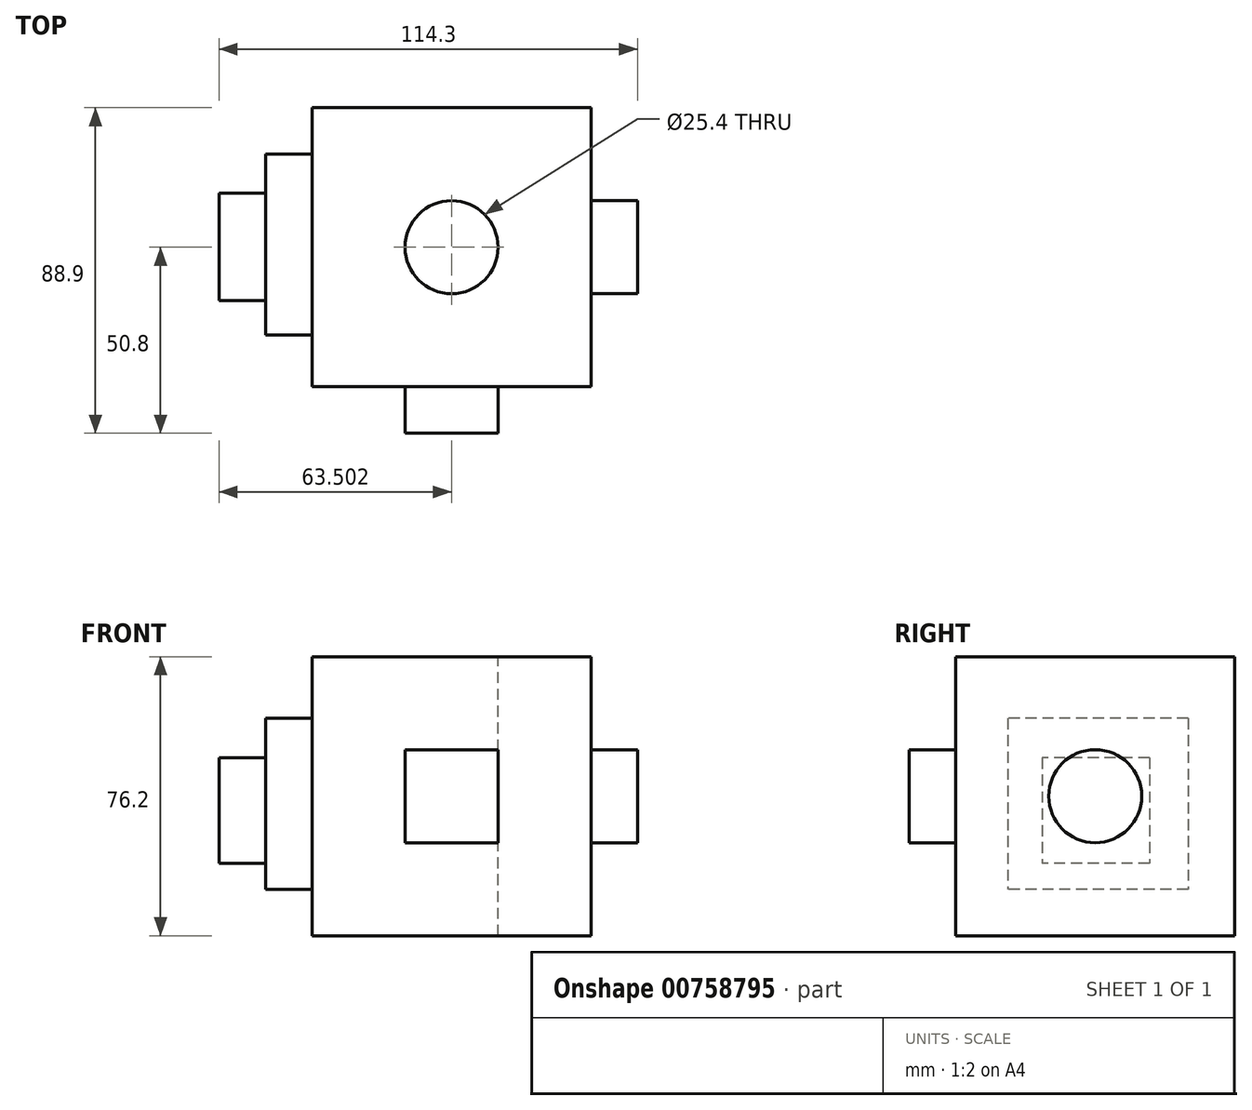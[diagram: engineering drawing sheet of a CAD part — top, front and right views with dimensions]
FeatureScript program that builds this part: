
annotation { "Feature Type Name" : "Feature", "Feature Type Description" : "" }
export const myFeature = defineFeature(function(context is Context, id is Id, definition is map)
    precondition{}
    {
        {
            var Q0;
            Q0=qCreatedBy(makeId("Front.planeOp"),FACE);
            var sketch = newSketch(context, id + "F0", { "sketchPlane" : qUnion([Q0])});
            skLineSegment(sketch, "E0.bottom", {"start": v(-34.38, 38.32) * mm, "end": v(41.82, 38.32) * mm});
            skLineSegment(sketch, "E0.top", {"start": v(-34.38, -37.88) * mm, "end": v(41.82, -37.88) * mm});
            skLineSegment(sketch, "E0.left", {"start": v(-34.38, 38.32) * mm, "end": v(-34.38, -37.88) * mm});
            skLineSegment(sketch, "E0.right", {"start": v(41.82, 38.32) * mm, "end": v(41.82, -37.88) * mm});
            skSolve(sketch);
        }
        {
            var Q0;
            Q0=makeQuery(id+"F0.imprint","IMPRINT",FACE,{"disambiguationData":[TD([[makeQuery(id+"F0.imprint","IMPRINT",EDGE,{"derivedFrom":sQuery(id+"F0.wireOp",EDGE,"E0.bottom")}),-1.0]])]});
            extrude(context, id + "F1", {"entities" : qUnion([Q0]), "depth" : 76.2 * mm, "offsetDistance" : 25.4 * mm});
        }
        {
            var Q0;
            Q0=makeQuery(id+"F1.opExtrude","CAP_FACE",FACE,{"disambiguationData":[OSD([sQuery(id+"F0.wireOp",EDGE,"E0.bottom"),sQuery(id+"F0.wireOp",EDGE,"E0.top"),sQuery(id+"F0.wireOp",EDGE,"E0.left"),sQuery(id+"F0.wireOp",EDGE,"E0.right")])],"isStart":false});
            var sketch = newSketch(context, id + "F2", { "sketchPlane" : qUnion([Q0])});
            skLineSegment(sketch, "E1.bottom", {"start": v(-8.98, 12.92) * mm, "end": v(16.42, 12.92) * mm});
            skLineSegment(sketch, "E1.top", {"start": v(-8.98, -12.48) * mm, "end": v(16.42, -12.48) * mm});
            skLineSegment(sketch, "E1.left", {"start": v(-8.98, 12.92) * mm, "end": v(-8.98, -12.48) * mm});
            skLineSegment(sketch, "E1.right", {"start": v(16.42, 12.92) * mm, "end": v(16.42, -12.48) * mm});
            skSolve(sketch);
        }
        {
            var Q0;
            Q0=makeQuery(id+"F2.imprint","IMPRINT",FACE,{"disambiguationData":[TD([[makeQuery(id+"F2.imprint","IMPRINT",EDGE,{"derivedFrom":sQuery(id+"F2.wireOp",EDGE,"E1.bottom")}),-1.0]])]});
            extrude(context, id + "F3", {"entities" : qUnion([Q0]), "operationType" : NewBodyOperationType.ADD, "depth" : 12.7 * mm, "offsetDistance" : 25.4 * mm});
        }
        {
            var Q0;
            Q0=makeQuery(id+"F1.opExtrude","SWEPT_FACE",FACE,{"disambiguationData":[OSD([sQuery(id+"F0.wireOp",EDGE,"E0.right")])]});
            var sketch = newSketch(context, id + "F4", { "sketchPlane" : qUnion([Q0])});
            skCircle(sketch, "E2", {"center": v(-38.1, 0.22) * mm, "radius": 12.7 * mm});
            skSolve(sketch);
        }
        {
            var Q0;
            Q0=makeQuery(id+"F4.imprint","IMPRINT",FACE,{"disambiguationData":[TD([[makeQuery(id+"F4.imprint","IMPRINT",EDGE,{"derivedFrom":sQuery(id+"F4.wireOp",EDGE,"E2")}),1.0]])]});
            extrude(context, id + "F5", {"entities" : qUnion([Q0]), "operationType" : NewBodyOperationType.ADD, "depth" : 12.7 * mm, "offsetDistance" : 25.4 * mm});
        }
        {
            var Q0;
            Q0=makeQuery(id+"F1.opExtrude","SWEPT_FACE",FACE,{"disambiguationData":[OSD([sQuery(id+"F0.wireOp",EDGE,"E0.bottom")])]});
            var sketch = newSketch(context, id + "F6", { "sketchPlane" : qUnion([Q0])});
            skPoint(sketch, "E3", {"position": v(3.72, -38.1) * mm});
            skSolve(sketch);
        }
        {
            var Q0;
            Q0=sQuery(id+"F6.wireOp",VERTEX,"E3");
            var Q1;
            Q1=makeQuery(id+"F1.opExtrude","SWEPT_BODY",BODY,{"disambiguationData":[OSD([sQuery(id+"F0.wireOp",EDGE,"E0.bottom"),sQuery(id+"F0.wireOp",EDGE,"E0.top"),sQuery(id+"F0.wireOp",EDGE,"E0.left"),sQuery(id+"F0.wireOp",EDGE,"E0.right")])]});
            hole(context, id + "F7", {"style" : HoleStyle.SIMPLE, "endStyle" : HoleEndStyle.THROUGH, "holeDiameter" : 25.4 * mm, "majorDiameter" : 6.35 * mm, "isTappedThrough" : true, "tappedDepth" : 12.7 * mm, "tapClearance" : 3, "locations" : qUnion([Q0]), "scope" : qUnion([Q1])});
        }
        {
            var Q0;
            Q0=makeQuery(id+"F1.opExtrude","SWEPT_FACE",FACE,{"disambiguationData":[OSD([sQuery(id+"F0.wireOp",EDGE,"E0.left")])]});
            var sketch = newSketch(context, id + "F8", { "sketchPlane" : qUnion([Q0])});
            skLineSegment(sketch, "E4.bottom", {"start": v(12.7, 21.52) * mm, "end": v(62.02, 21.52) * mm});
            skLineSegment(sketch, "E4.top", {"start": v(12.7, -25.18) * mm, "end": v(62.02, -25.18) * mm});
            skLineSegment(sketch, "E4.left", {"start": v(12.7, 21.52) * mm, "end": v(12.7, -25.18) * mm});
            skLineSegment(sketch, "E4.right", {"start": v(62.02, 21.52) * mm, "end": v(62.02, -25.18) * mm});
            skSolve(sketch);
        }
        {
            var Q0;
            Q0=makeQuery(id+"F8.imprint","IMPRINT",FACE,{"disambiguationData":[TD([[makeQuery(id+"F8.imprint","IMPRINT",EDGE,{"derivedFrom":sQuery(id+"F8.wireOp",EDGE,"E4.bottom")}),-1.0]])]});
            extrude(context, id + "F9", {"entities" : qUnion([Q0]), "operationType" : NewBodyOperationType.ADD, "depth" : 12.7 * mm, "offsetDistance" : 25.4 * mm});
        }
        {
            var Q0;
            Q0=makeQuery(id+"F9.opExtrude","CAP_FACE",FACE,{"disambiguationData":[OSD([sQuery(id+"F8.wireOp",EDGE,"E4.bottom"),sQuery(id+"F8.wireOp",EDGE,"E4.top"),sQuery(id+"F8.wireOp",EDGE,"E4.left"),sQuery(id+"F8.wireOp",EDGE,"E4.right")])],"isStart":false});
            var sketch = newSketch(context, id + "F10", { "sketchPlane" : qUnion([Q0])});
            skLineSegment(sketch, "E5.bottom", {"start": v(23.3, 10.68) * mm, "end": v(52.62, 10.68) * mm});
            skLineSegment(sketch, "E5.top", {"start": v(23.3, -18.18) * mm, "end": v(52.62, -18.18) * mm});
            skLineSegment(sketch, "E5.left", {"start": v(23.3, 10.68) * mm, "end": v(23.3, -18.18) * mm});
            skLineSegment(sketch, "E5.right", {"start": v(52.62, 10.68) * mm, "end": v(52.62, -18.18) * mm});
            skSolve(sketch);
        }
        {
            var Q0;
            Q0=makeQuery(id+"F10.imprint","IMPRINT",FACE,{"disambiguationData":[TD([[makeQuery(id+"F10.imprint","IMPRINT",EDGE,{"derivedFrom":sQuery(id+"F10.wireOp",EDGE,"E5.bottom")}),-1.0]])]});
            extrude(context, id + "F11", {"entities" : qUnion([Q0]), "operationType" : NewBodyOperationType.ADD, "depth" : 12.7 * mm, "offsetDistance" : 25.4 * mm});
        }
    });
